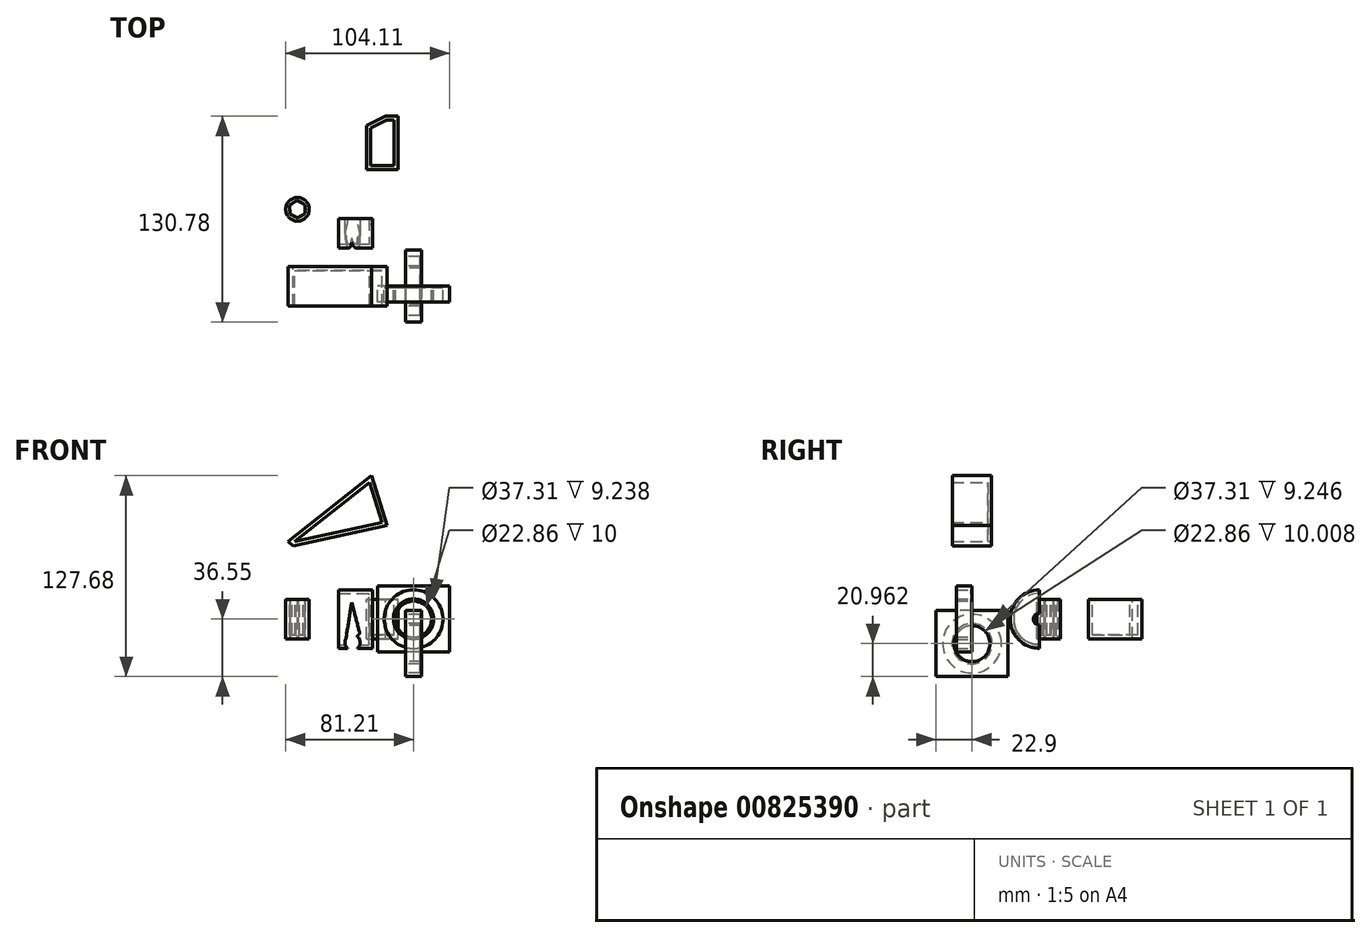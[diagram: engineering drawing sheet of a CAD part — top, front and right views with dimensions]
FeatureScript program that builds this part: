
annotation { "Feature Type Name" : "Feature", "Feature Type Description" : "" }
export const myFeature = defineFeature(function(context is Context, id is Id, definition is map)
    precondition{}
    {
        {
            var Q0;
            Q0=qCreatedBy(makeId("Front.planeOp"),FACE);
            var sketch = newSketch(context, id + "F0", { "sketchPlane" : qUnion([Q0])});
            skLineSegment(sketch, "E0.bottom", {"start": v(22.9, -20.96) * mm, "end": v(-22.9, -20.96) * mm});
            skLineSegment(sketch, "E0.top", {"start": v(22.9, 20.96) * mm, "end": v(-22.9, 20.96) * mm});
            skLineSegment(sketch, "E0.left", {"start": v(22.9, -20.96) * mm, "end": v(22.9, 20.96) * mm});
            skLineSegment(sketch, "E0.right", {"start": v(-22.9, -20.96) * mm, "end": v(-22.9, 20.96) * mm});
            skPoint(sketch, "E0.middle", {"position": v(0, 0) * mm});
            skCircle(sketch, "E1", {"center": v(0, 0) * mm, "radius": 18.66 * mm});
            skCircle(sketch, "E2", {"center": v(0, 0) * mm, "radius": 12.8 * mm});
            skLineSegment(sketch, "E3.bottom", {"start": v(-22.9, -20.96) * mm, "end": v(22.9, -20.96) * mm});
            skLineSegment(sketch, "E3.top", {"start": v(-22.9, 20.96) * mm, "end": v(22.9, 20.96) * mm});
            skSolve(sketch);
        }
        {
            var Q0;
            Q0=makeQuery(id+"F0.imprint","IMPRINT",FACE,{"disambiguationData":[TD([[makeQuery(id+"F0.imprint","IMPRINT",EDGE,{"derivedFrom":sQuery(id+"F0.wireOp",EDGE,"E0.bottom")}),-1.0]])]});
            var Q1;
            Q1=makeQuery(id+"F0.imprint","IMPRINT",FACE,{"disambiguationData":[TD([[makeQuery(id+"F0.imprint","IMPRINT",EDGE,{"derivedFrom":sQuery(id+"F0.wireOp",EDGE,"E1")}),-1.0]])]});
            extrude(context, id + "F1", {"entities" : qUnion([Q0, Q1]), "depth" : 10 * mm, "offsetDistance" : 25.4 * mm});
        }
        {
            var Q0;
            Q0=makeQuery(id+"F0.imprint","IMPRINT",FACE,{"disambiguationData":[TD([[makeQuery(id+"F0.imprint","IMPRINT",EDGE,{"derivedFrom":sQuery(id+"F0.wireOp",EDGE,"E2")}),1.0]])]});
            extrude(context, id + "F2", {"entities" : qUnion([Q0]), "depth" : 10 * mm, "offsetDistance" : 25.4 * mm});
        }
        {
            var Q0;
            Q0=makeQuery(id+"F0.imprint","IMPRINT",FACE,{"disambiguationData":[TD([[makeQuery(id+"F0.imprint","IMPRINT",EDGE,{"derivedFrom":sQuery(id+"F0.wireOp",EDGE,"E2")}),1.0]])]});
            var Q1;
            Q1=makeQuery(id+"F0.imprint","IMPRINT",FACE,{"disambiguationData":[TD([[makeQuery(id+"F0.imprint","IMPRINT",EDGE,{"derivedFrom":sQuery(id+"F0.wireOp",EDGE,"E1")}),1.0]])]});
            extrude(context, id + "F3", {"entities" : qUnion([Q0, Q1]), "operationType" : NewBodyOperationType.ADD, "depth" : 0.76 * mm, "offsetDistance" : 25.4 * mm});
        }
        {
            var Q0;
            Q0=sQuery(id+"F0.wireOp",VERTEX,"E0.middle");
            var Q1;
            Q1=makeQuery(id+"F1.opExtrude","SWEPT_BODY",BODY,{"disambiguationData":[OSD([sQuery(id+"F0.wireOp",EDGE,"E1"),sQuery(id+"F0.wireOp",EDGE,"E0.bottom"),sQuery(id+"F0.wireOp",EDGE,"E0.top"),sQuery(id+"F0.wireOp",EDGE,"E0.left"),sQuery(id+"F0.wireOp",EDGE,"E0.right")])]});
            hole(context, id + "F4", {"style" : HoleStyle.SIMPLE, "endStyle" : HoleEndStyle.THROUGH, "oppositeDirection" : true, "holeDiameter" : 22.86 * mm, "majorDiameter" : 6.35 * mm, "isTappedThrough" : true, "tappedDepth" : 12.7 * mm, "tapClearance" : 3, "locations" : qUnion([Q0]), "scope" : qUnion([Q1])});
        }
        {
            var Q0;
            Q0=qCreatedBy(makeId("Right.planeOp"),FACE);
            var sketch = newSketch(context, id + "F5", { "sketchPlane" : qUnion([Q0])});
            skLineSegment(sketch, "E4.bottom", {"start": v(22.9, -36.55) * mm, "end": v(-22.9, -36.55) * mm});
            skLineSegment(sketch, "E4.top", {"start": v(22.9, 5.37) * mm, "end": v(-22.9, 5.37) * mm});
            skLineSegment(sketch, "E4.left", {"start": v(22.9, -36.55) * mm, "end": v(22.9, 5.37) * mm});
            skLineSegment(sketch, "E4.right", {"start": v(-22.9, -36.55) * mm, "end": v(-22.9, 5.37) * mm});
            skPoint(sketch, "E4.middle", {"position": v(0, -15.59) * mm});
            skCircle(sketch, "E5", {"center": v(0, -15.59) * mm, "radius": 18.66 * mm});
            skCircle(sketch, "E6", {"center": v(0, -15.59) * mm, "radius": 12.8 * mm});
            skLineSegment(sketch, "E7.bottom", {"start": v(-22.9, -36.55) * mm, "end": v(22.9, -36.55) * mm});
            skLineSegment(sketch, "E7.top", {"start": v(-22.9, 5.37) * mm, "end": v(22.9, 5.37) * mm});
            skSolve(sketch);
        }
        {
            var Q0;
            Q0 = qSketchRegion(id + "F5", true);
            extrude(context, id + "F6", {"entities" : qUnion([Q0]), "endBound" : BoundingType.SYMMETRIC, "depth" : 10 * mm, "offsetDistance" : 25.4 * mm});
        }
        {
            var Q0;
            Q0=qCreatedBy(makeId("Right.planeOp"),FACE);
            var sketch = newSketch(context, id + "F7", { "sketchPlane" : qUnion([Q0])});
            skCircle(sketch, "E8", {"center": v(0, -15.59) * mm, "radius": 12.8 * mm});
            skCircle(sketch, "E9", {"center": v(0, -15.59) * mm, "radius": 11.43 * mm});
            skSolve(sketch);
        }
        {
            var Q0;
            Q0 = qSketchRegion(id + "F7", true);
            extrude(context, id + "F8", {"entities" : qUnion([Q0]), "endBound" : BoundingType.SYMMETRIC, "depth" : 10 * mm, "offsetDistance" : 25.4 * mm});
        }
        {
            var Q0;
            Q0=makeQuery(id+"F6.opExtrude","CAP_FACE",FACE,{"disambiguationData":[OSD([sQuery(id+"F5.wireOp",EDGE,"E5"),sQuery(id+"F5.wireOp",EDGE,"E4.bottom"),sQuery(id+"F5.wireOp",EDGE,"E4.top"),sQuery(id+"F5.wireOp",EDGE,"E4.left"),sQuery(id+"F5.wireOp",EDGE,"E4.right")])],"isStart":false});
            var sketch = newSketch(context, id + "F9", { "sketchPlane" : qUnion([Q0])});
            skLineSegment(sketch, "E10.bottom", {"start": v(-22.9, 5.37) * mm, "end": v(22.9, 5.37) * mm});
            skLineSegment(sketch, "E10.top", {"start": v(-22.9, -36.55) * mm, "end": v(22.9, -36.55) * mm});
            skLineSegment(sketch, "E10.left", {"start": v(-22.9, 5.37) * mm, "end": v(-22.9, -36.55) * mm});
            skLineSegment(sketch, "E10.right", {"start": v(22.9, 5.37) * mm, "end": v(22.9, -36.55) * mm});
            skPoint(sketch, "E10.middle", {"position": v(0, -15.59) * mm});
            skCircle(sketch, "E11", {"center": v(0, -15.59) * mm, "radius": 12.65 * mm});
            skSolve(sketch);
        }
        {
            var Q0;
            Q0 = qSketchRegion(id + "F9", true);
            extrude(context, id + "F10", {"entities" : qUnion([Q0]), "operationType" : NewBodyOperationType.ADD, "oppositeDirection" : true, "depth" : 0.76 * mm, "offsetDistance" : 25.4 * mm});
        }
        {
            var Q0;
            Q0=qCreatedBy(makeId("Top.planeOp"),FACE);
            var sketch = newSketch(context, id + "F11", { "sketchPlane" : qUnion([Q0])});
            skCircle(sketch, "E12", {"center": v(-73.71, 48.81) * mm, "radius": 7.5 * mm});
            skLineSegment(sketch, "E13", {"start": v(-29.73, 74.07) * mm, "end": v(-9.73, 74.07) * mm});
            skLineSegment(sketch, "E14", {"start": v(-9.73, 107.88) * mm, "end": v(-9.73, 74.07) * mm});
            skLineSegment(sketch, "E15", {"start": v(-9.73, 107.88) * mm, "end": v(-17.78, 107.88) * mm});
            skLineSegment(sketch, "E16", {"start": v(-29.73, 74.07) * mm, "end": v(-29.73, 101.9) * mm});
            skLineSegment(sketch, "E17", {"start": v(-17.78, 107.88) * mm, "end": v(-29.73, 101.9) * mm});
            skSolve(sketch);
        }
        {
            var Q0;
            Q0 = qSketchRegion(id + "F11", true);
            extrude(context, id + "F12", {"entities" : qUnion([Q0]), "endBound" : BoundingType.SYMMETRIC, "oppositeDirection" : true, "depth" : 25 * mm, "offsetDistance" : 25 * mm});
        }
        {
            var Q0;
            Q0=qCreatedBy(makeId("Front.planeOp"),FACE);
            var sketch = newSketch(context, id + "F13", { "sketchPlane" : qUnion([Q0])});
            skLineSegment(sketch, "E18", {"start": v(-80.87, 48.35) * mm, "end": v(-26.58, 91.13) * mm});
            skLineSegment(sketch, "E19", {"start": v(-26.58, 91.13) * mm, "end": v(-16.86, 59.53) * mm});
            skLineSegment(sketch, "E20", {"start": v(-16.86, 59.53) * mm, "end": v(-76.5, 46.57) * mm});
            skLineSegment(sketch, "E21", {"start": v(-76.5, 46.57) * mm, "end": v(-79.6, 49.36) * mm});
            skSolve(sketch);
        }
        {
            var Q0;
            Q0 = qSketchRegion(id + "F13", true);
            extrude(context, id + "F14", {"entities" : qUnion([Q0]), "operationType" : NewBodyOperationType.ADD, "endBound" : BoundingType.SYMMETRIC, "depth" : 25 * mm, "offsetDistance" : 25 * mm});
        }
        {
            var Q0;
            Q0=makeQuery(id+"F14.boolean.opBoolean","MERGE",FACE,{"derivedFrom":[makeQuery(id+"F12.opExtrude","CAP_FACE",FACE,{"disambiguationData":[OSD([sQuery(id+"F11.wireOp",EDGE,"E12")])],"isStart":true}),makeQuery(id+"F12.opExtrude","CAP_FACE",FACE,{"disambiguationData":[OSD([sQuery(id+"F11.wireOp",EDGE,"E13"),sQuery(id+"F11.wireOp",EDGE,"E14"),sQuery(id+"F11.wireOp",EDGE,"E15"),sQuery(id+"F11.wireOp",EDGE,"E16"),sQuery(id+"F11.wireOp",EDGE,"E17")])],"isStart":true}),makeQuery(id+"F14.opExtrude","CAP_FACE",FACE,{"disambiguationData":[OSD([sQuery(id+"F13.wireOp",EDGE,"E18"),sQuery(id+"F13.wireOp",EDGE,"E19"),sQuery(id+"F13.wireOp",EDGE,"E20"),sQuery(id+"F13.wireOp",EDGE,"E21")])],"isStart":false})]});
            shell(context, id + "F15", {"entities" : qUnion([Q0]), "thickness" : 2.5 * mm});
        }
        {
            var Q0;
            Q0=qCreatedBy(makeId("Top.planeOp"),FACE);
            var sketch = newSketch(context, id + "F16", { "sketchPlane" : qUnion([Q0])});
            skLineSegment(sketch, "E22", {"start": v(-26, 24.27) * mm, "end": v(-47.6, 24.27) * mm});
            skLineSegment(sketch, "E23", {"start": v(-47.6, 24.27) * mm, "end": v(-47.6, 26.5) * mm});
            skLineSegment(sketch, "E24", {"start": v(-47.6, 26.5) * mm, "end": v(-28.23, 26.5) * mm});
            skLineSegment(sketch, "E25", {"start": v(-26, 39) * mm, "end": v(-26, 24.27) * mm});
            skLineSegment(sketch, "E26", {"start": v(-50.98, 42.76) * mm, "end": v(-22.96, 42.76) * mm, "construction": true});
            skLineSegment(sketch, "E27", {"start": v(-26, 39) * mm, "end": v(-28.23, 39) * mm});
            skLineSegment(sketch, "E28", {"start": v(-28.23, 39) * mm, "end": v(-28.23, 26.5) * mm});
            skPoint(sketch, "E29.orphan", {"position": v(-26, 26.5) * mm});
            skSolve(sketch);
        }
        {
            var Q0;
            Q0 = qSketchRegion(id + "F16", true);
            var Q1;
            Q1=sQuery(id+"F16.wireOp",EDGE,"E26");
            revolve(context, id + "F17", {"surfaceOperationType" : NewSurfaceOperationType.NEW, "entities" : qUnion([Q0]), "axis" : qUnion([Q1]), "revolveType" : RevolveType.SYMMETRIC, "angle" : 180 * degree});
        }
        {
            var Q0;
            Q0=qCreatedBy(makeId("Front.planeOp"),FACE);
            var sketch = newSketch(context, id + "F18", { "sketchPlane" : qUnion([Q0])});
            skArc(sketch, "E30", {"start": v(-42.92, -12.31) * mm, "mid": v(-37.73, -19.57) * mm, "end": v(-35.98, -10.82) * mm});
            skLineSegment(sketch, "E31", {"start": v(-42.92, -12.31) * mm, "end": v(-39.24, 10.7) * mm});
            skLineSegment(sketch, "E32", {"start": v(-39.24, 10.7) * mm, "end": v(-34.15, -9.08) * mm});
            skLineSegment(sketch, "E33", {"start": v(-34.15, -9.08) * mm, "end": v(-35.98, -10.82) * mm});
            skSolve(sketch);
        }
        {
            var Q0;
            Q0 = qSketchRegion(id + "F18", true);
            extrude(context, id + "F19", {"entities" : qUnion([Q0]), "operationType" : NewBodyOperationType.REMOVE, "endBound" : BoundingType.THROUGH_ALL, "oppositeDirection" : true, "depth" : 25 * mm, "offsetDistance" : 25 * mm});
        }
        {
            var Q0;
            Q0=makeQuery(id+"F12.opExtrude","CAP_FACE",FACE,{"disambiguationData":[OSD([sQuery(id+"F11.wireOp",EDGE,"E12")])],"isStart":false});
            var sketch = newSketch(context, id + "F20", { "sketchPlane" : qUnion([Q0])});
            skLineSegment(sketch, "E34.0", {"start": v(-74, -54.36) * mm, "end": v(-78.66, -51.33) * mm});
            skLineSegment(sketch, "E34.1", {"start": v(-78.66, -51.33) * mm, "end": v(-78.37, -45.79) * mm});
            skLineSegment(sketch, "E34.2", {"start": v(-78.37, -45.79) * mm, "end": v(-73.42, -43.27) * mm});
            skLineSegment(sketch, "E34.3", {"start": v(-73.42, -43.27) * mm, "end": v(-68.76, -46.3) * mm});
            skLineSegment(sketch, "E34.4", {"start": v(-68.76, -46.3) * mm, "end": v(-69.06, -51.84) * mm});
            skLineSegment(sketch, "E34.5", {"start": v(-69.06, -51.84) * mm, "end": v(-74, -54.36) * mm});
            skPoint(sketch, "E34.0.midPoint", {"position": v(-76.33, -52.84) * mm});
            skSolve(sketch);
        }
        {
            var Q0;
            Q0 = qSketchRegion(id + "F20", true);
            extrude(context, id + "F21", {"entities" : qUnion([Q0]), "operationType" : NewBodyOperationType.REMOVE, "endBound" : BoundingType.THROUGH_ALL, "oppositeDirection" : true, "depth" : 25 * mm, "offsetDistance" : 25 * mm});
        }
    });
